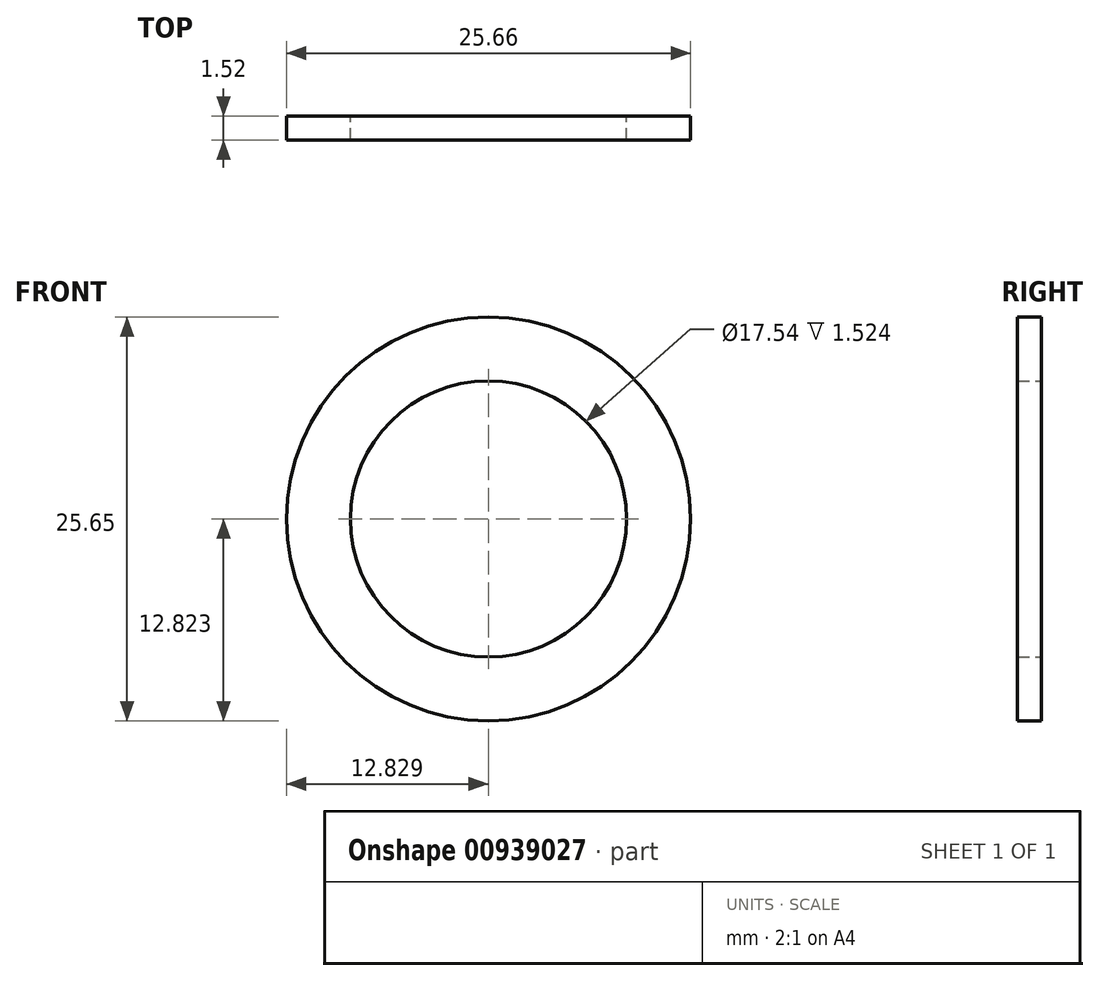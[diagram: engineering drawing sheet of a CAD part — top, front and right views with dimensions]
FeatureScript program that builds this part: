
annotation { "Feature Type Name" : "Feature", "Feature Type Description" : "" }
export const myFeature = defineFeature(function(context is Context, id is Id, definition is map)
    precondition{}
    {
        {
            var Q0;
            Q0=qCreatedBy(makeId("Front.planeOp"),FACE);
            var sketch = newSketch(context, id + "F0", { "sketchPlane" : qUnion([Q0])});
            skCircle(sketch, "E0", {"center": v(-42.72, 39.88) * mm, "radius": 12.83 * mm});
            skCircle(sketch, "E1", {"center": v(-42.72, 39.88) * mm, "radius": 8.77 * mm});
            skSolve(sketch);
        }
        {
            var Q0;
            Q0 = qSketchRegion(id + "F0", true);
            extrude(context, id + "F1", {"entities" : qUnion([Q0]), "depth" : 1.52 * mm, "offsetDistance" : 25.4 * mm});
        }
    });
